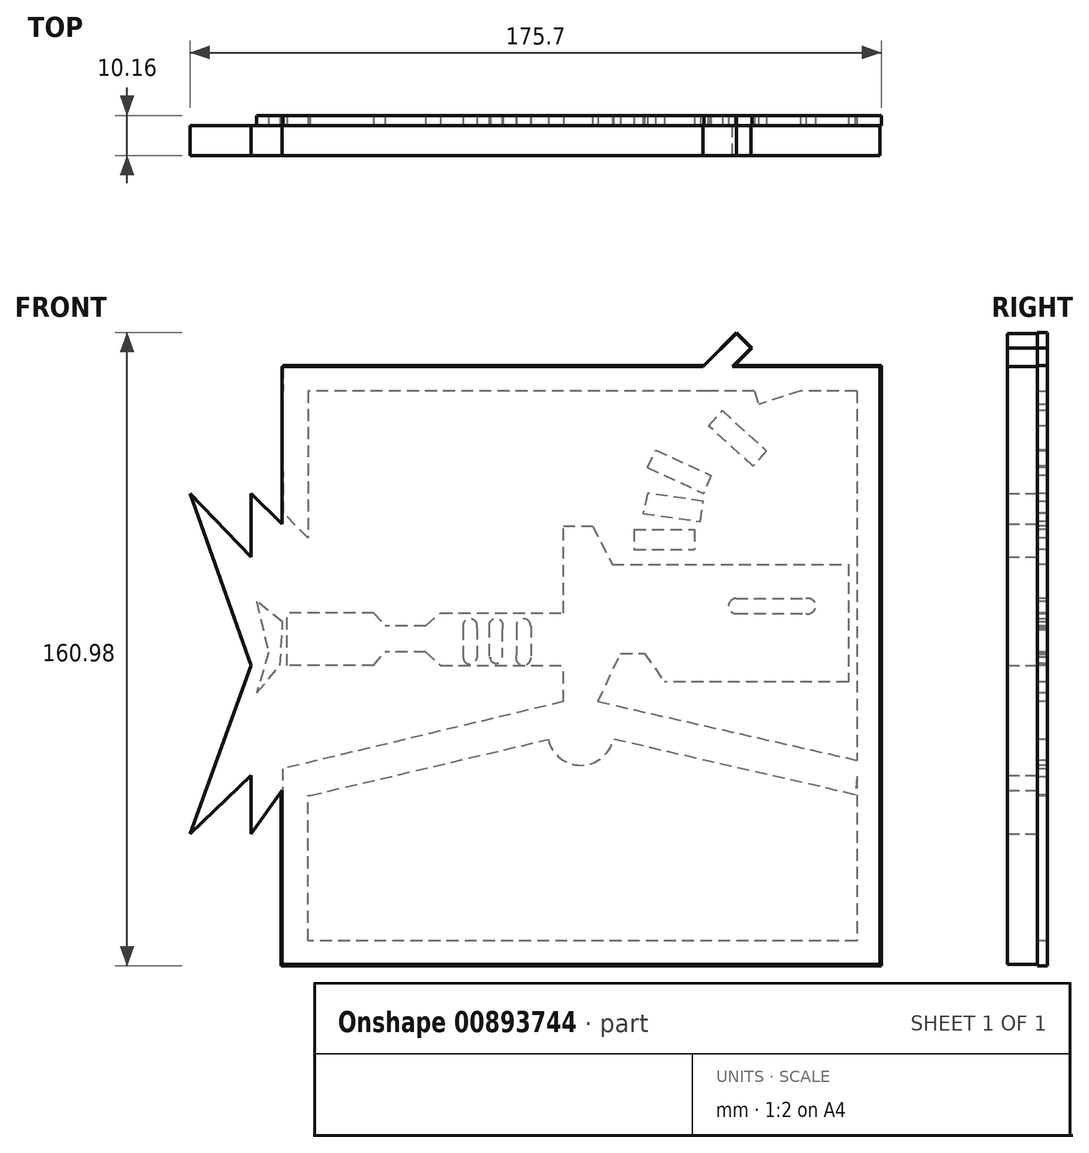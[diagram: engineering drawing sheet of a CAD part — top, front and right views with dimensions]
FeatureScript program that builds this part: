
annotation { "Feature Type Name" : "Feature", "Feature Type Description" : "" }
export const myFeature = defineFeature(function(context is Context, id is Id, definition is map)
    precondition{}
    {
        {
            var Q0;
            Q0=qCreatedBy(makeId("Front.planeOp"),FACE);
            var sketch = newSketch(context, id + "F0", { "sketchPlane" : qUnion([Q0])});
            skLineSegment(sketch, "E0.bottom", {"start": v(-75.93, 75.93) * mm, "end": v(75.93, 75.93) * mm});
            skLineSegment(sketch, "E0.top", {"start": v(-75.93, -75.93) * mm, "end": v(75.93, -75.93) * mm});
            skLineSegment(sketch, "E0.left", {"start": v(-75.93, 75.93) * mm, "end": v(-75.93, -75.93) * mm});
            skLineSegment(sketch, "E0.right", {"start": v(75.93, 75.93) * mm, "end": v(75.93, -75.93) * mm});
            skLineSegment(sketch, "E1", {"start": v(-75.93, 35.9) * mm, "end": v(-83.84, 43.73) * mm});
            skLineSegment(sketch, "E2", {"start": v(-83.84, 43.73) * mm, "end": v(-83.84, 27.52) * mm});
            skLineSegment(sketch, "E3", {"start": v(-83.84, 27.52) * mm, "end": v(-99.3, 43.73) * mm});
            skLineSegment(sketch, "E4", {"start": v(-99.3, 43.73) * mm, "end": v(-83.84, 0) * mm});
            skLineSegment(sketch, "E5", {"start": v(-83.84, 0) * mm, "end": v(-99.3, -42.72) * mm});
            skLineSegment(sketch, "E6", {"start": v(-99.3, -42.72) * mm, "end": v(-83.84, -27.96) * mm});
            skLineSegment(sketch, "E7", {"start": v(-83.84, -27.96) * mm, "end": v(-83.84, -42.72) * mm});
            skLineSegment(sketch, "E8", {"start": v(-83.84, -42.72) * mm, "end": v(-75.93, -31.72) * mm});
            skLineSegment(sketch, "E9", {"start": v(28.88, 73.73) * mm, "end": v(32.61, 70) * mm});
            skLineSegment(sketch, "E10", {"start": v(32.61, 70) * mm, "end": v(43.23, 80.63) * mm});
            skLineSegment(sketch, "E11", {"start": v(43.23, 80.63) * mm, "end": v(39.5, 84.35) * mm});
            skLineSegment(sketch, "E12", {"start": v(39.5, 84.35) * mm, "end": v(28.88, 73.73) * mm});
            skSolve(sketch);
        }
        {
            var Q0;
            Q0 = qSketchRegion(id + "F0", true);
            extrude(context, id + "F1", {"entities" : qUnion([Q0]), "depth" : 7.62 * mm, "offsetDistance" : 25.4 * mm});
        }
        {
            var Q0;
            Q0=qCreatedBy(makeId("Front.planeOp"),FACE);
            var sketch = newSketch(context, id + "F2", { "sketchPlane" : qUnion([Q0])});
            skLineSegment(sketch, "E13.bottom", {"start": v(76.4, 76.18) * mm, "end": v(70.14, 76.18) * mm});
            skLineSegment(sketch, "E13.top", {"start": v(76.4, -76.36) * mm, "end": v(70.14, -76.36) * mm});
            skLineSegment(sketch, "E13.left", {"start": v(76.4, 76.18) * mm, "end": v(76.4, -76.36) * mm});
            skLineSegment(sketch, "E13.right", {"start": v(70.14, 76.18) * mm, "end": v(70.14, -76.36) * mm});
            skLineSegment(sketch, "E14.bottom", {"start": v(76.4, -76.36) * mm, "end": v(-76.14, -76.36) * mm});
            skLineSegment(sketch, "E14.top", {"start": v(76.4, -69.93) * mm, "end": v(-76.14, -69.93) * mm});
            skLineSegment(sketch, "E14.left", {"start": v(76.4, -76.36) * mm, "end": v(76.4, -69.93) * mm});
            skLineSegment(sketch, "E14.right", {"start": v(-76.14, -76.36) * mm, "end": v(-76.14, -69.93) * mm});
            skLineSegment(sketch, "E15.bottom", {"start": v(76.4, 76.18) * mm, "end": v(-75.64, 76.18) * mm});
            skLineSegment(sketch, "E15.top", {"start": v(76.4, 69.75) * mm, "end": v(-75.64, 69.75) * mm});
            skLineSegment(sketch, "E15.left", {"start": v(76.4, 76.18) * mm, "end": v(76.4, 69.75) * mm});
            skLineSegment(sketch, "E15.right", {"start": v(-75.64, 76.18) * mm, "end": v(-75.64, 69.75) * mm});
            skLineSegment(sketch, "E16.bottom", {"start": v(-75.64, 76.18) * mm, "end": v(-69.32, 76.18) * mm});
            skLineSegment(sketch, "E16.right", {"start": v(-69.32, 76.18) * mm, "end": v(-69.32, 32.47) * mm});
            skLineSegment(sketch, "E17.bottom", {"start": v(-76.14, -76.36) * mm, "end": v(-69.32, -76.36) * mm});
            skLineSegment(sketch, "E17.top", {"start": v(-76.14, -32.69) * mm, "end": v(-69.32, -32.69) * mm});
            skLineSegment(sketch, "E17.left", {"start": v(-76.14, -76.36) * mm, "end": v(-76.14, -32.69) * mm});
            skLineSegment(sketch, "E17.right", {"start": v(-69.32, -76.36) * mm, "end": v(-69.32, -32.69) * mm});
            skLineSegment(sketch, "E18", {"start": v(-69.32, 32.47) * mm, "end": v(-75.55, 38.76) * mm});
            skLineSegment(sketch, "E19", {"start": v(-75.55, 38.76) * mm, "end": v(-75.64, 69.75) * mm});
            skLineSegment(sketch, "E20", {"start": v(38.97, 76.18) * mm, "end": v(32.38, 69.75) * mm});
            skLineSegment(sketch, "E21", {"start": v(32.38, 69.75) * mm, "end": v(28.83, 73.38) * mm});
            skLineSegment(sketch, "E22", {"start": v(28.83, 73.38) * mm, "end": v(31.7, 76.18) * mm});
            skSolve(sketch);
        }
        {
            var Q0;
            {var subQ0=sQuery(id+"F2.wireOp",EDGE,"E13.top");var subQ1=sQuery(id+"F2.wireOp",EDGE,"E13.left");var subQ2=sQuery(id+"F2.wireOp",EDGE,"E14.top");var subQ5=sQuery(id+"F2.wireOp",EDGE,"E13.right");var subQ7=makeQuery(id+"F2.imprint","INTERSECT",VERTEX,{"derivedFrom":[subQ5,subQ2]});var subQ13=sQuery(id+"F2.wireOp",EDGE,"E20");var subQ15=makeQuery(id+"F2.imprint","IMPRINT",EDGE,{"derivedFrom":subQ13});var subQ16=sQuery(id+"F2.wireOp",EDGE,"E21");var subQ17=makeQuery(id+"F2.imprint","IMPRINT",EDGE,{"derivedFrom":subQ16});var subQ19=sQuery(id+"F2.wireOp",EDGE,"E13.bottom");var subQ20=sQuery(id+"F2.wireOp",EDGE,"E15.top");var subQ21=makeQuery(id+"F2.imprint","INTERSECT",VERTEX,{"derivedFrom":[subQ1,subQ20]});var subQ32=sQuery(id+"F2.wireOp",EDGE,"E15.right");var subQ34=sQuery(id+"F2.wireOp",EDGE,"E18");var subQ35=sQuery(id+"F2.wireOp",EDGE,"E14.right");var subQ42=sQuery(id+"F2.wireOp",EDGE,"E17.top");Q0=qUnion([makeQuery(id+"F2.imprint","IMPRINT",FACE,{"disambiguationData":[TD([[makeQuery(id+"F2.imprint","IMPRINT",EDGE,{"disambiguationData":[TD([[subQ7,-1.0]])],"derivedFrom":subQ2}),1.0]])]}),makeQuery(id+"F2.imprint","IMPRINT",FACE,{"disambiguationData":[TD([[makeQuery(id+"F2.imprint","IMPRINT",EDGE,{"derivedFrom":subQ32}),1.0]])]}),makeQuery(id+"F2.imprint","IMPRINT",FACE,{"disambiguationData":[TD([[makeQuery(id+"F2.imprint","IMPRINT",EDGE,{"derivedFrom":subQ42}),-1.0]])]}),makeQuery(id+"F2.imprint","IMPRINT",FACE,{"disambiguationData":[TD([[makeQuery(id+"F2.imprint","IMPRINT",EDGE,{"disambiguationData":[TD([[subQ21,-1.0]])],"derivedFrom":subQ1}),-1.0]])]}),makeQuery(id+"F2.imprint","IMPRINT",FACE,{"disambiguationData":[TD([[makeQuery(id+"F2.imprint","IMPRINT",EDGE,{"derivedFrom":subQ35}),-1.0]])]}),makeQuery(id+"F2.imprint","IMPRINT",FACE,{"disambiguationData":[TD([[makeQuery(id+"F2.imprint","IMPRINT",EDGE,{"derivedFrom":subQ34}),-1.0]])]}),makeQuery(id+"F2.imprint","IMPRINT",FACE,{"disambiguationData":[TD([[subQ15,1.0]])]}),makeQuery(id+"F2.imprint","IMPRINT",FACE,{"disambiguationData":[TD([[subQ17,1.0]])]}),makeQuery(id+"F2.imprint","IMPRINT",FACE,{"disambiguationData":[TD([[makeQuery(id+"F2.imprint","IMPRINT",EDGE,{"derivedFrom":subQ19}),1.0]])]}),makeQuery(id+"F2.imprint","IMPRINT",FACE,{"disambiguationData":[TD([[subQ15,-1.0]])]}),makeQuery(id+"F2.imprint","IMPRINT",FACE,{"disambiguationData":[TD([[makeQuery(id+"F2.imprint","IMPRINT",EDGE,{"derivedFrom":subQ0}),-1.0]])]})]);}
            extrude(context, id + "F3", {"entities" : qUnion([Q0]), "operationType" : NewBodyOperationType.ADD, "oppositeDirection" : true, "depth" : 2.54 * mm, "offsetDistance" : 25.4 * mm});
        }
        {
            var Q0;
            Q0=qCreatedBy(makeId("Front.planeOp"),FACE);
            var sketch = newSketch(context, id + "F4", { "sketchPlane" : qUnion([Q0])});
            skLineSegment(sketch, "E23", {"start": v(-68.79, -33) * mm, "end": v(0, -16.84) * mm});
            skLineSegment(sketch, "E24", {"start": v(-4.42, -9.15) * mm, "end": v(-75.74, -26.23) * mm});
            skLineSegment(sketch, "E25", {"start": v(-75.74, -26.23) * mm, "end": v(-75.74, -32.83) * mm});
            skLineSegment(sketch, "E26", {"start": v(69.68, -32.83) * mm, "end": v(0, -16.84) * mm});
            skLineSegment(sketch, "E27", {"start": v(4.42, -9.15) * mm, "end": v(70.55, -24.14) * mm});
            skLineSegment(sketch, "E28", {"start": v(-4.42, -9.15) * mm, "end": v(-4.42, 35.45) * mm});
            skLineSegment(sketch, "E29", {"start": v(-4.42, 35.45) * mm, "end": v(2.96, 35.45) * mm});
            skLineSegment(sketch, "E30", {"start": v(2.96, 35.45) * mm, "end": v(8, 25.72) * mm});
            skLineSegment(sketch, "E31", {"start": v(8, 25.72) * mm, "end": v(67.94, 25.72) * mm});
            skLineSegment(sketch, "E32", {"start": v(67.94, 25.72) * mm, "end": v(67.94, -4.16) * mm});
            skLineSegment(sketch, "E33", {"start": v(67.94, -4.16) * mm, "end": v(21.2, -4.16) * mm});
            skLineSegment(sketch, "E34", {"start": v(4.42, -9.15) * mm, "end": v(10.09, 3.14) * mm});
            skLineSegment(sketch, "E35", {"start": v(10.09, 3.14) * mm, "end": v(16.17, 3.14) * mm});
            skLineSegment(sketch, "E36", {"start": v(16.17, 3.14) * mm, "end": v(21.2, -4.16) * mm});
            skCircle(sketch, "E37", {"center": v(39.45, 15.12) * mm, "radius": 1.92 * mm});
            skCircle(sketch, "E38", {"center": v(57.7, 15.12) * mm, "radius": 1.98 * mm});
            skLineSegment(sketch, "E39", {"start": v(39.45, 13.2) * mm, "end": v(58.18, 13.2) * mm});
            skLineSegment(sketch, "E40", {"start": v(39.45, 17.04) * mm, "end": v(57.2, 17.04) * mm});
            skLineSegment(sketch, "E41.left", {"start": v(-4.42, 1.92) * mm, "end": v(-4.42, 13.39) * mm});
            skCircle(sketch, "E42", {"center": v(0, -16.84) * mm, "radius": 8.5 * mm});
            skLineSegment(sketch, "E43.left", {"start": v(-4.42, 13.39) * mm, "end": v(-4.42, 0) * mm});
            skLineSegment(sketch, "E43.right", {"start": v(-35.6, 13.39) * mm, "end": v(-35.6, 0) * mm});
            skLineSegment(sketch, "E44.bottom", {"start": v(-35.6, 10.09) * mm, "end": v(-52.63, 10.09) * mm});
            skLineSegment(sketch, "E44.top", {"start": v(-35.6, 3.48) * mm, "end": v(-52.63, 3.48) * mm});
            skLineSegment(sketch, "E44.left", {"start": v(-35.6, 10.09) * mm, "end": v(-35.6, 3.48) * mm});
            skLineSegment(sketch, "E44.right", {"start": v(-52.63, 10.09) * mm, "end": v(-52.63, 3.48) * mm});
            skLineSegment(sketch, "E45.left", {"start": v(-35.6, 0) * mm, "end": v(-35.6, 13.39) * mm});
            skLineSegment(sketch, "E45.right", {"start": v(-52.63, 0) * mm, "end": v(-52.63, 13.39) * mm});
            skLineSegment(sketch, "E46.bottom", {"start": v(-52.63, 0) * mm, "end": v(-74.7, 0) * mm});
            skLineSegment(sketch, "E46.top", {"start": v(-52.63, 13.39) * mm, "end": v(-74.7, 13.39) * mm});
            skLineSegment(sketch, "E46.right", {"start": v(-74.7, 0) * mm, "end": v(-74.7, 13.39) * mm});
            skLineSegment(sketch, "E47", {"start": v(-52.63, 0) * mm, "end": v(-49.68, 3.48) * mm});
            skLineSegment(sketch, "E48", {"start": v(-49.68, 3.48) * mm, "end": v(-49.68, 10.09) * mm});
            skLineSegment(sketch, "E49", {"start": v(-52.63, 13.39) * mm, "end": v(-49.68, 10.09) * mm});
            skLineSegment(sketch, "E50", {"start": v(-39.43, 10.09) * mm, "end": v(-35.6, 13.39) * mm});
            skLineSegment(sketch, "E51", {"start": v(-39.43, 10.09) * mm, "end": v(-39.43, 3.48) * mm});
            skLineSegment(sketch, "E52", {"start": v(-39.43, 3.48) * mm, "end": v(-35.6, 0) * mm});
            skLineSegment(sketch, "E53.bottom", {"start": v(-35.6, 13.39) * mm, "end": v(-4.42, 13.39) * mm});
            skLineSegment(sketch, "E53.top", {"start": v(-35.6, 0) * mm, "end": v(-4.42, 0) * mm});
            skLineSegment(sketch, "E54", {"start": v(-75.74, -32.83) * mm, "end": v(-68.79, -33) * mm});
            skLineSegment(sketch, "E55", {"start": v(70.55, -24.14) * mm, "end": v(69.68, -32.83) * mm});
            skCircle(sketch, "E56", {"center": v(-28.13, 10.09) * mm, "radius": 1.81 * mm});
            skCircle(sketch, "E57", {"center": v(-21.53, 10.09) * mm, "radius": 1.81 * mm});
            skCircle(sketch, "E58", {"center": v(-14.58, 10.09) * mm, "radius": 1.81 * mm});
            skLineSegment(sketch, "E59.bottom", {"start": v(-28.13, 10.09) * mm, "end": v(-29.87, 10.09) * mm});
            skLineSegment(sketch, "E59.top", {"start": v(-28.13, 2.06) * mm, "end": v(-29.87, 2.06) * mm});
            skLineSegment(sketch, "E59.right", {"start": v(-29.87, 10.09) * mm, "end": v(-29.87, 2.06) * mm});
            skLineSegment(sketch, "E60.bottom", {"start": v(-28.13, 10.09) * mm, "end": v(-26.4, 10.09) * mm});
            skLineSegment(sketch, "E60.top", {"start": v(-28.13, 2.04) * mm, "end": v(-26.4, 2.04) * mm});
            skLineSegment(sketch, "E60.right", {"start": v(-26.4, 10.09) * mm, "end": v(-26.4, 2.04) * mm});
            skLineSegment(sketch, "E61.bottom", {"start": v(-23.35, 10.09) * mm, "end": v(-21.53, 10.09) * mm});
            skLineSegment(sketch, "E61.top", {"start": v(-23.35, 2.01) * mm, "end": v(-21.53, 2.01) * mm});
            skLineSegment(sketch, "E61.left", {"start": v(-23.35, 10.09) * mm, "end": v(-23.35, 2.01) * mm});
            skLineSegment(sketch, "E62.bottom", {"start": v(-21.53, 10.09) * mm, "end": v(-20.01, 10.09) * mm});
            skLineSegment(sketch, "E62.top", {"start": v(-21.53, 2) * mm, "end": v(-20.01, 2) * mm});
            skLineSegment(sketch, "E62.right", {"start": v(-20.01, 10.09) * mm, "end": v(-20.01, 2) * mm});
            skLineSegment(sketch, "E63.bottom", {"start": v(-14.58, 10.09) * mm, "end": v(-16.32, 10.09) * mm});
            skLineSegment(sketch, "E63.top", {"start": v(-14.58, 1.99) * mm, "end": v(-16.32, 1.99) * mm});
            skLineSegment(sketch, "E63.right", {"start": v(-16.32, 10.09) * mm, "end": v(-16.32, 1.99) * mm});
            skLineSegment(sketch, "E64.bottom", {"start": v(-14.58, 10.09) * mm, "end": v(-12.67, 10.09) * mm});
            skLineSegment(sketch, "E64.top", {"start": v(-14.58, 1.97) * mm, "end": v(-12.67, 1.97) * mm});
            skLineSegment(sketch, "E64.right", {"start": v(-12.67, 10.09) * mm, "end": v(-12.67, 1.97) * mm});
            skCircle(sketch, "E65", {"center": v(-28.13, 2.06) * mm, "radius": 1.74 * mm});
            skCircle(sketch, "E66", {"center": v(-21.53, 2.01) * mm, "radius": 1.47 * mm});
            skCircle(sketch, "E67", {"center": v(-14.58, 1.99) * mm, "radius": 1.91 * mm});
            skSolve(sketch);
        }
        {
            var Q0;
            Q0 = qSketchRegion(id + "F4", true);
            extrude(context, id + "F5", {"entities" : qUnion([Q0]), "operationType" : NewBodyOperationType.ADD, "oppositeDirection" : true, "depth" : 2.54 * mm, "offsetDistance" : 25.4 * mm});
        }
        {
            var Q0;
            Q0=qCreatedBy(makeId("Front.planeOp"),FACE);
            var sketch = newSketch(context, id + "F6", { "sketchPlane" : qUnion([Q0])});
            skLineSegment(sketch, "E68.bottom", {"start": v(13.52, 34.52) * mm, "end": v(28.81, 34.52) * mm});
            skLineSegment(sketch, "E68.top", {"start": v(13.52, 29.48) * mm, "end": v(28.81, 29.48) * mm});
            skLineSegment(sketch, "E68.left", {"start": v(13.52, 34.52) * mm, "end": v(13.52, 29.48) * mm});
            skLineSegment(sketch, "E68.right", {"start": v(28.81, 34.52) * mm, "end": v(28.81, 29.48) * mm});
            skLineSegment(sketch, "E69", {"start": v(15.78, 38.69) * mm, "end": v(30.38, 36.6) * mm});
            skLineSegment(sketch, "E70", {"start": v(30.38, 36.6) * mm, "end": v(31.1, 41.73) * mm});
            skLineSegment(sketch, "E71", {"start": v(31.1, 41.73) * mm, "end": v(16.93, 43.76) * mm});
            skLineSegment(sketch, "E72", {"start": v(16.93, 43.76) * mm, "end": v(15.78, 38.69) * mm});
            skLineSegment(sketch, "E73", {"start": v(16.93, 50.33) * mm, "end": v(31.1, 43.76) * mm});
            skLineSegment(sketch, "E74", {"start": v(31.1, 43.76) * mm, "end": v(16.93, 50.33) * mm});
            skLineSegment(sketch, "E75", {"start": v(16.93, 50.33) * mm, "end": v(19, 54.8) * mm});
            skLineSegment(sketch, "E76", {"start": v(19, 54.8) * mm, "end": v(33.08, 48.27) * mm});
            skLineSegment(sketch, "E77", {"start": v(33.08, 48.27) * mm, "end": v(31.1, 43.76) * mm});
            skLineSegment(sketch, "E78", {"start": v(32.46, 60.92) * mm, "end": v(35.93, 64.75) * mm});
            skLineSegment(sketch, "E79", {"start": v(35.93, 64.75) * mm, "end": v(32.46, 60.92) * mm});
            skLineSegment(sketch, "E80", {"start": v(35.93, 64.75) * mm, "end": v(47.2, 54.5) * mm});
            skLineSegment(sketch, "E81", {"start": v(47.2, 54.5) * mm, "end": v(43.74, 50.69) * mm});
            skLineSegment(sketch, "E82", {"start": v(43.74, 50.69) * mm, "end": v(32.46, 60.92) * mm});
            skLineSegment(sketch, "E83", {"start": v(43.74, 71) * mm, "end": v(45.14, 66.3) * mm});
            skLineSegment(sketch, "E84", {"start": v(43.74, 71) * mm, "end": v(58.35, 75.38) * mm});
            skLineSegment(sketch, "E85", {"start": v(58.35, 75.38) * mm, "end": v(59.67, 71) * mm});
            skLineSegment(sketch, "E86", {"start": v(59.67, 71) * mm, "end": v(45.14, 66.3) * mm});
            skLineSegment(sketch, "E87", {"start": v(28.72, 73.64) * mm, "end": v(39.52, 84.62) * mm});
            skLineSegment(sketch, "E88", {"start": v(39.52, 84.62) * mm, "end": v(43.49, 80.72) * mm});
            skLineSegment(sketch, "E89", {"start": v(43.49, 80.72) * mm, "end": v(32.57, 69.6) * mm});
            skLineSegment(sketch, "E90", {"start": v(32.57, 69.6) * mm, "end": v(28.72, 73.64) * mm});
            skSolve(sketch);
        }
        {
            var Q0;
            Q0 = qSketchRegion(id + "F6", true);
            extrude(context, id + "F7", {"entities" : qUnion([Q0]), "operationType" : NewBodyOperationType.ADD, "oppositeDirection" : true, "depth" : 2.54 * mm, "offsetDistance" : 25.4 * mm});
        }
        {
            var Q0;
            Q0=qCreatedBy(makeId("Front.planeOp"),FACE);
            var sketch = newSketch(context, id + "F8", { "sketchPlane" : qUnion([Q0])});
            skLineSegment(sketch, "E91", {"start": v(-75.83, 11.13) * mm, "end": v(-82.35, 16.35) * mm});
            skLineSegment(sketch, "E92", {"start": v(-82.35, 16.35) * mm, "end": v(-79.37, 3.3) * mm});
            skLineSegment(sketch, "E93", {"start": v(-79.37, 3.3) * mm, "end": v(-82.35, -6.94) * mm});
            skLineSegment(sketch, "E94", {"start": v(-82.35, -6.94) * mm, "end": v(-76.39, 0) * mm});
            skLineSegment(sketch, "E95", {"start": v(-76.39, 0) * mm, "end": v(-75.83, 9.45) * mm});
            skLineSegment(sketch, "E96", {"start": v(-75.83, 9.45) * mm, "end": v(-75.83, 11.13) * mm});
            skSolve(sketch);
        }
        {
            var Q0;
            Q0 = qSketchRegion(id + "F8", true);
            extrude(context, id + "F9", {"entities" : qUnion([Q0]), "operationType" : NewBodyOperationType.ADD, "oppositeDirection" : true, "depth" : 2.54 * mm, "offsetDistance" : 25.4 * mm});
        }
    });
